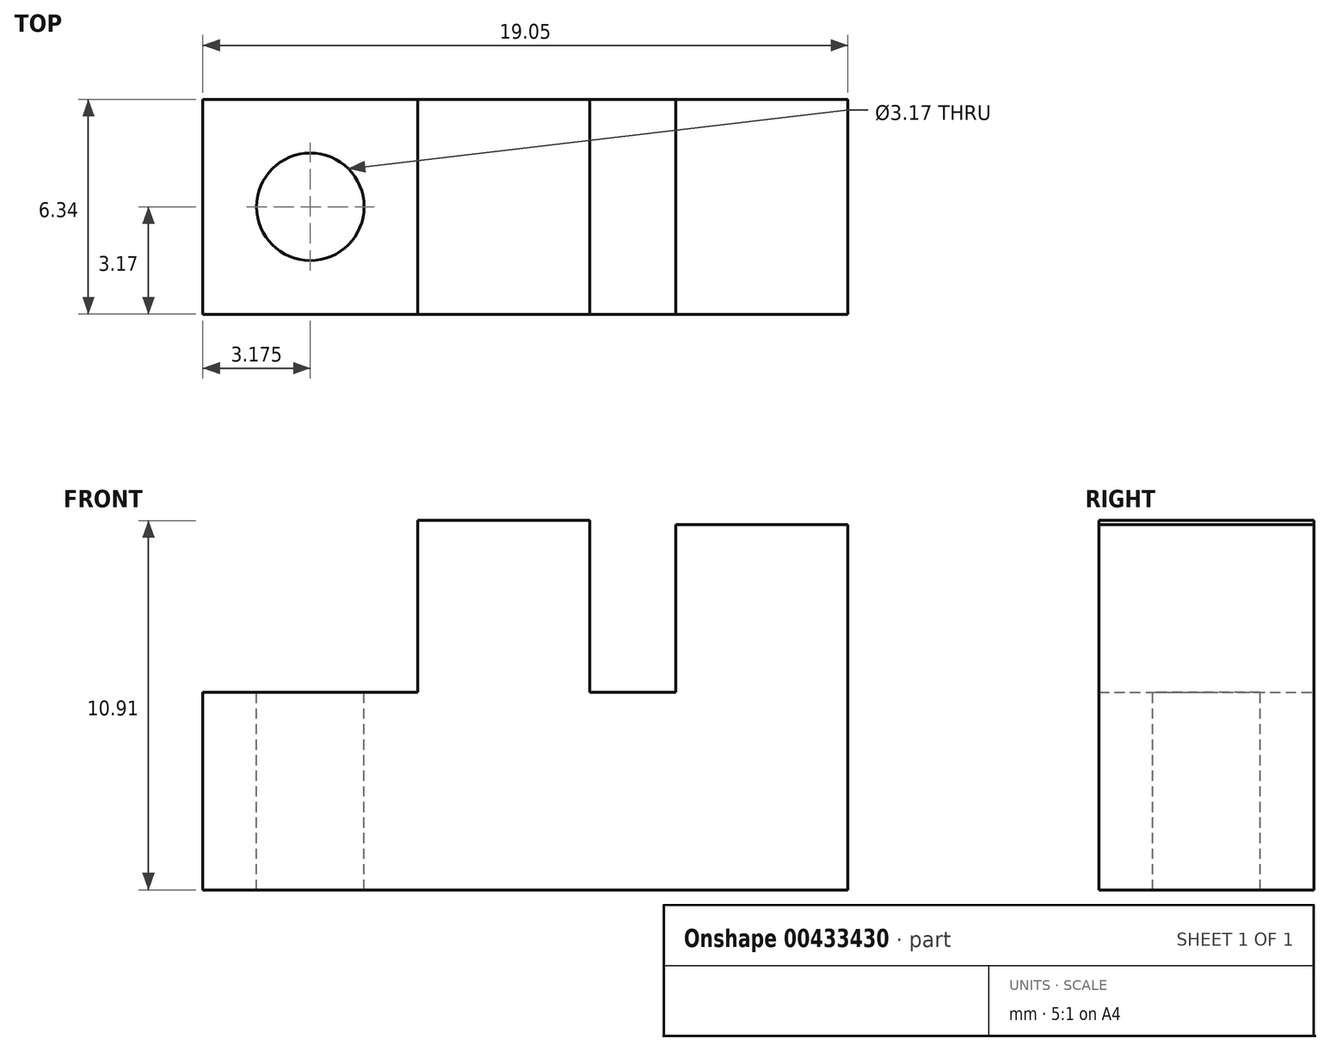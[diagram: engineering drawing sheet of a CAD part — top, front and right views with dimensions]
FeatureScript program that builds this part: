
annotation { "Feature Type Name" : "Feature", "Feature Type Description" : "" }
export const myFeature = defineFeature(function(context is Context, id is Id, definition is map)
    precondition{}
    {
        {
            var Q0;
            Q0=qCreatedBy(makeId("Front.planeOp"),FACE);
            var sketch = newSketch(context, id + "F0", { "sketchPlane" : qUnion([Q0])});
            skLineSegment(sketch, "E0", {"start": v(6.35, 0) * mm, "end": v(-12.7, 0) * mm});
            skLineSegment(sketch, "E1", {"start": v(-12.7, 0) * mm, "end": v(-12.7, 5.83) * mm});
            skLineSegment(sketch, "E2", {"start": v(-12.7, 5.83) * mm, "end": v(-6.35, 5.83) * mm});
            skLineSegment(sketch, "E3", {"start": v(-6.35, 5.83) * mm, "end": v(-6.35, 10.91) * mm});
            skLineSegment(sketch, "E4", {"start": v(0, 0) * mm, "end": v(0, 11.67) * mm, "construction": true});
            skLineSegment(sketch, "E5", {"start": v(-6.35, 10.91) * mm, "end": v(-1.27, 10.91) * mm});
            skLineSegment(sketch, "E6", {"start": v(-1.27, 10.91) * mm, "end": v(-1.27, 5.83) * mm});
            skPoint(sketch, "E6.endSnap0", {"position": v(0, 5.83) * mm});
            skLineSegment(sketch, "E7", {"start": v(-1.27, 5.83) * mm, "end": v(1.27, 5.83) * mm});
            skLineSegment(sketch, "E8", {"start": v(1.27, 5.83) * mm, "end": v(1.27, 10.8) * mm});
            skLineSegment(sketch, "E9", {"start": v(1.27, 10.8) * mm, "end": v(6.35, 10.8) * mm});
            skLineSegment(sketch, "E10", {"start": v(6.35, 10.8) * mm, "end": v(6.35, 0) * mm});
            skSolve(sketch);
        }
        {
            var Q0;
            Q0 = qSketchRegion(id + "F0", true);
            extrude(context, id + "F1", {"entities" : qUnion([Q0]), "endBound" : BoundingType.SYMMETRIC, "depth" : 6.35 * mm});
        }
        {
            var Q0;
            Q0=makeQuery(id+"F1.opExtrude","SWEPT_FACE",FACE,{"disambiguationData":[OSD([sQuery(id+"F0.wireOp",EDGE,"E2")])]});
            cPlane(context, id + "F2", {"entities" : qUnion([Q0]), "cplaneType" : CPlaneType.OFFSET, "offset" : 0 * mm, "width" : 152.4 * mm, "height" : 152.4 * mm});
        }
        {
            var Q0;
            Q0=qCreatedBy(id+"F2.planeOp",FACE);
            var sketch = newSketch(context, id + "F3", { "sketchPlane" : qUnion([Q0])});
            skPoint(sketch, "E11", {"position": v(-9.53, 0) * mm});
            skSolve(sketch);
        }
        {
            var Q0;
            Q0=sQuery(id+"F3.wireOp",VERTEX,"E11");
            var Q1;
            Q1=makeQuery(id+"F1.opExtrude","SWEPT_BODY",BODY,{"disambiguationData":[OSD([sQuery(id+"F0.wireOp",EDGE,"E0"),sQuery(id+"F0.wireOp",EDGE,"E1"),sQuery(id+"F0.wireOp",EDGE,"E2"),sQuery(id+"F0.wireOp",EDGE,"E3"),sQuery(id+"F0.wireOp",EDGE,"E5"),sQuery(id+"F0.wireOp",EDGE,"E6"),sQuery(id+"F0.wireOp",EDGE,"E7"),sQuery(id+"F0.wireOp",EDGE,"E8"),sQuery(id+"F0.wireOp",EDGE,"E9"),sQuery(id+"F0.wireOp",EDGE,"E10")])]});
            hole(context, id + "F4", {"style" : HoleStyle.SIMPLE, "endStyle" : HoleEndStyle.THROUGH, "holeDiameter" : 3.17 * mm, "isTappedThrough" : true, "tappedDepth" : 12.7 * mm, "tapClearance" : 3, "locations" : qUnion([Q0]), "scope" : qUnion([Q1])});
        }
    });
